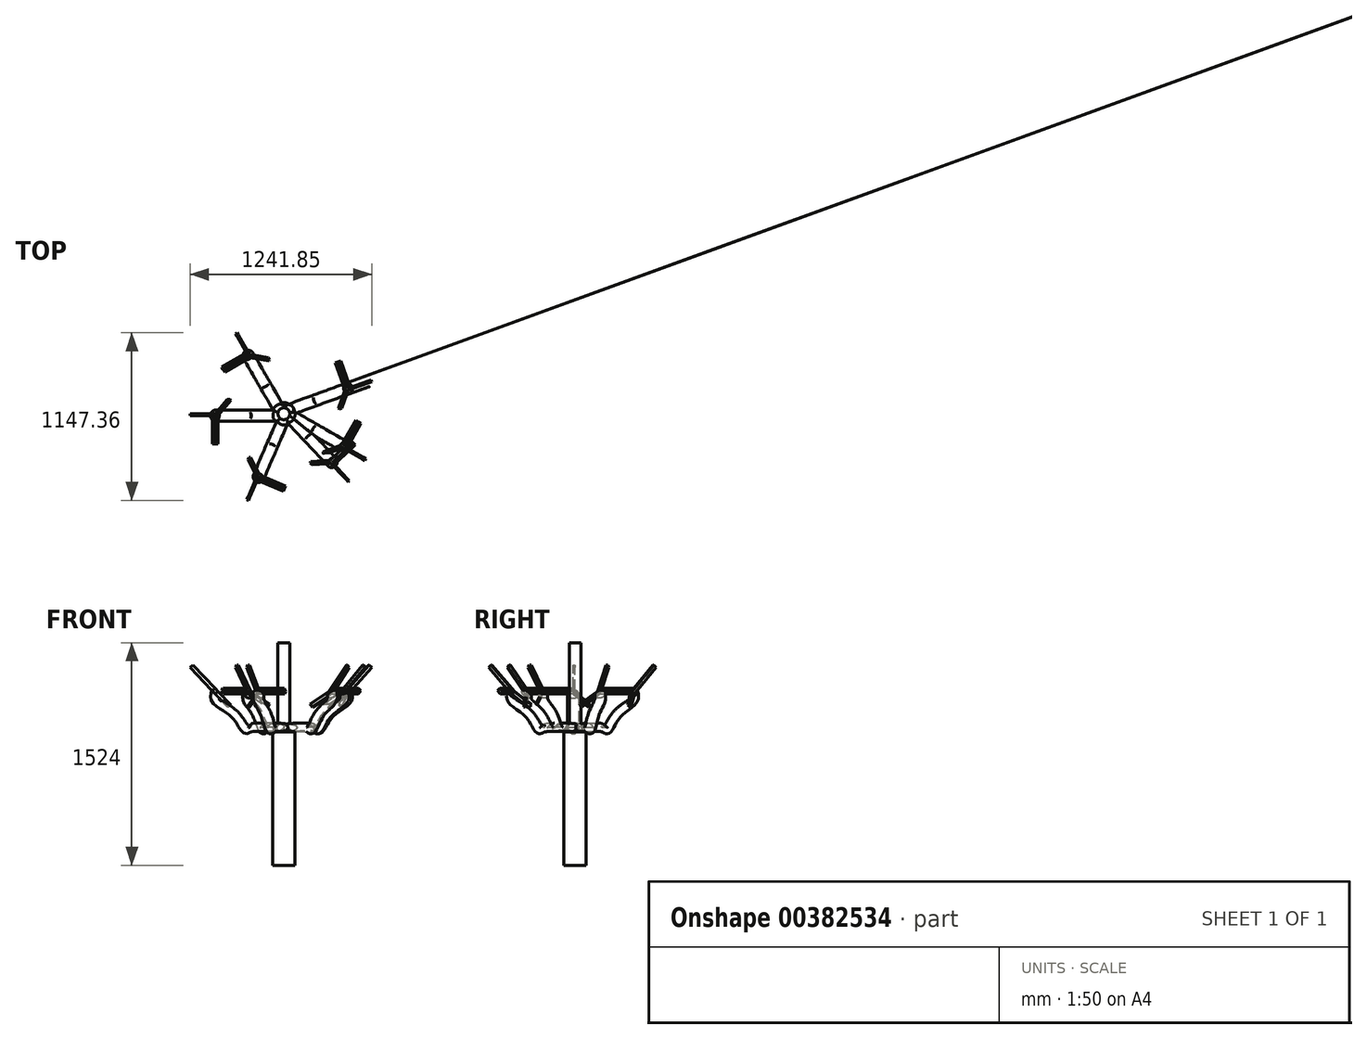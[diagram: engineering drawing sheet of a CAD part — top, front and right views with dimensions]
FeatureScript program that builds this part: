
annotation { "Feature Type Name" : "Feature", "Feature Type Description" : "" }
export const myFeature = defineFeature(function(context is Context, id is Id, definition is map)
    precondition{}
    {
        {
            var Q0;
            Q0=qCreatedBy(makeId("Top.planeOp"),FACE);
            var sketch = newSketch(context, id + "F0", { "sketchPlane" : qUnion([Q0])});
            skCircle(sketch, "E0", {"center": v(0, 0) * mm, "radius": 76.2 * mm});
            skSolve(sketch);
        }
        {
            var Q0;
            Q0 = qSketchRegion(id + "F0", true);
            extrude(context, id + "F1", {"entities" : qUnion([Q0]), "depth" : 914.4 * mm});
        }
        {
            var Q0;
            Q0=makeQuery(id+"F1.opExtrude","CAP_FACE",FACE,{"disambiguationData":[OSD([sQuery(id+"F0.wireOp",EDGE,"E0")])],"isStart":false});
            var sketch = newSketch(context, id + "F2", { "sketchPlane" : qUnion([Q0])});
            skCircle(sketch, "E1", {"center": v(-35.92, -12.7) * mm, "radius": 38.1 * mm});
            skLineSegment(sketch, "E2", {"start": v(-76.2, 40.6) * mm, "end": v(-76.2, -48.89) * mm});
            skSolve(sketch);
        }
        {
            var Q0;
            Q0=makeQuery(id+"F2.imprint","IMPRINT",FACE,{"disambiguationData":[TD([[makeQuery(id+"F2.imprint","IMPRINT",EDGE,{"derivedFrom":sQuery(id+"F2.wireOp",EDGE,"E1")}),1.0]])]});
            var Q1;
            Q1=sQuery(id+"F2.wireOp",EDGE,"E2");
            revolve(context, id + "F3", {"entities" : qUnion([Q0]), "axis" : qUnion([Q1]), "revolveType" : RevolveType.ONE_DIRECTION, "angle" : 45 * degree});
        }
        {
            var Q0;
            Q0=qCreatedBy(makeId("Front.planeOp"),FACE);
            var sketch = newSketch(context, id + "F4", { "sketchPlane" : qUnion([Q0])});
            skFitSpline(sketch, "E3", {"points": [v(-46.1, 946.37) * mm, v(-221.46, 943.93) * mm, v(-256.37, 939.27) * mm, v(-335.13, 1035.72) * mm, v(-457.3, 1130.55) * mm, v(-465.33, 1170.74) * mm], "startDerivative": vector(-779, 33.25) * mm, "endDerivative": vector(22.57, 307.36) * mm});
            skSolve(sketch);
        }
        {
            var Q0;
            Q0=makeQuery(id+"F3.opRevolve","CAP_FACE",FACE,{"disambiguationData":[OSD([sQuery(id+"F2.wireOp",EDGE,"E1")])],"isStart":false});
            var Q1;
            Q1=sQuery(id+"F4.wireOp",EDGE,"E3");
            sweep(context, id + "F5", {"operationType" : NewBodyOperationType.ADD, "profiles" : qUnion([Q0]), "path" : qUnion([Q1])});
        }
        {
            var Q0;
            Q0=makeQuery(id+"F5.opSweep","CAP_FACE",FACE,{"disambiguationData":[OSD([sQuery(id+"F2.wireOp",EDGE,"E1"),sQuery(id+"F4.wireOp",VERTEX,"E3.end")])],"isStart":false});
            var sketch = newSketch(context, id + "F6", { "sketchPlane" : qUnion([Q0])});
            skLineSegment(sketch, "E4.bottom", {"start": v(-12.7, 1175.23) * mm, "end": v(0, 1175.23) * mm});
            skLineSegment(sketch, "E4.top", {"start": v(-12.7, 1425.51) * mm, "end": v(0, 1425.51) * mm});
            skLineSegment(sketch, "E4.left", {"start": v(-12.7, 1175.23) * mm, "end": v(-12.7, 1425.51) * mm});
            skLineSegment(sketch, "E4.right", {"start": v(0, 1175.23) * mm, "end": v(0, 1425.51) * mm});
            skLineSegment(sketch, "E5.bottom", {"start": v(-12.7, 1175.23) * mm, "end": v(-207.3, 1175.23) * mm});
            skLineSegment(sketch, "E5.top", {"start": v(-12.7, 1206.07) * mm, "end": v(-207.3, 1206.07) * mm});
            skLineSegment(sketch, "E5.left", {"start": v(-12.7, 1175.23) * mm, "end": v(-12.7, 1206.07) * mm});
            skLineSegment(sketch, "E5.right", {"start": v(-207.3, 1175.23) * mm, "end": v(-207.3, 1206.07) * mm});
            skLineSegment(sketch, "E6", {"start": v(-12.7, 1175.23) * mm, "end": v(91.62, 1049.2) * mm});
            skLineSegment(sketch, "E7", {"start": v(91.62, 1049.2) * mm, "end": v(99.42, 1055.66) * mm});
            skLineSegment(sketch, "E8", {"start": v(99.42, 1055.66) * mm, "end": v(0, 1175.23) * mm});
            skSolve(sketch);
        }
        {
            var Q0;
            Q0 = qSketchRegion(id + "F6", true);
            extrude(context, id + "F7", {"entities" : qUnion([Q0]), "operationType" : NewBodyOperationType.ADD, "depth" : 25.4 * mm});
        }
        {
            var Q0;
            Q0=makeQuery(id+"F5.opSweep","SWEPT_BODY",BODY,{"disambiguationData":[OSD([sQuery(id+"F2.wireOp",EDGE,"E1"),sQuery(id+"F4.wireOp",EDGE,"E3")])]});
            var Q1;
            Q1=makeQuery(id+"F3.opRevolve","SWEPT_BODY",BODY,{"disambiguationData":[OSD([sQuery(id+"F2.wireOp",EDGE,"E1")])]});
            var Q2;
            Q2=makeQuery(id+"F1.opExtrude","CAP_EDGE",EDGE,{"disambiguationData":[OSD([sQuery(id+"F0.wireOp",EDGE,"E0")])],"isStart":false});
            circularPattern(context, id + "F8", {"entities" : qUnion([Q0, Q1]), "axis" : qUnion([Q2]), "angle" : 300 * degree, "instanceCount" : 3, "equalSpace" : true});
        }
        {
            var Q0;
            Q0=makeQuery(id+"F3.opRevolve","SWEPT_BODY",BODY,{"disambiguationData":[OSD([sQuery(id+"F2.wireOp",EDGE,"E1")])]});
            var Q1;
            Q1=makeQuery(id+"F1.opExtrude","CAP_EDGE",EDGE,{"disambiguationData":[OSD([sQuery(id+"F0.wireOp",EDGE,"E0")])],"isStart":false});
            circularPattern(context, id + "F9", {"entities" : qUnion([Q0]), "axis" : qUnion([Q1]), "angle" : 200 * degree, "instanceCount" : 4, "equalSpace" : true});
        }
        {
            var Q0;
            Q0=makeQuery(id+"F1.opExtrude","CAP_FACE",FACE,{"disambiguationData":[OSD([sQuery(id+"F0.wireOp",EDGE,"E0")])],"isStart":false});
            var sketch = newSketch(context, id + "F10", { "sketchPlane" : qUnion([Q0])});
            skCircle(sketch, "E9", {"center": v(0, 0) * mm, "radius": 40.51 * mm});
            skSolve(sketch);
        }
        {
            var Q0;
            Q0 = qSketchRegion(id + "F10", true);
            extrude(context, id + "F11", {"entities" : qUnion([Q0]), "operationType" : NewBodyOperationType.ADD, "depth" : 609.6 * mm});
        }
    });
